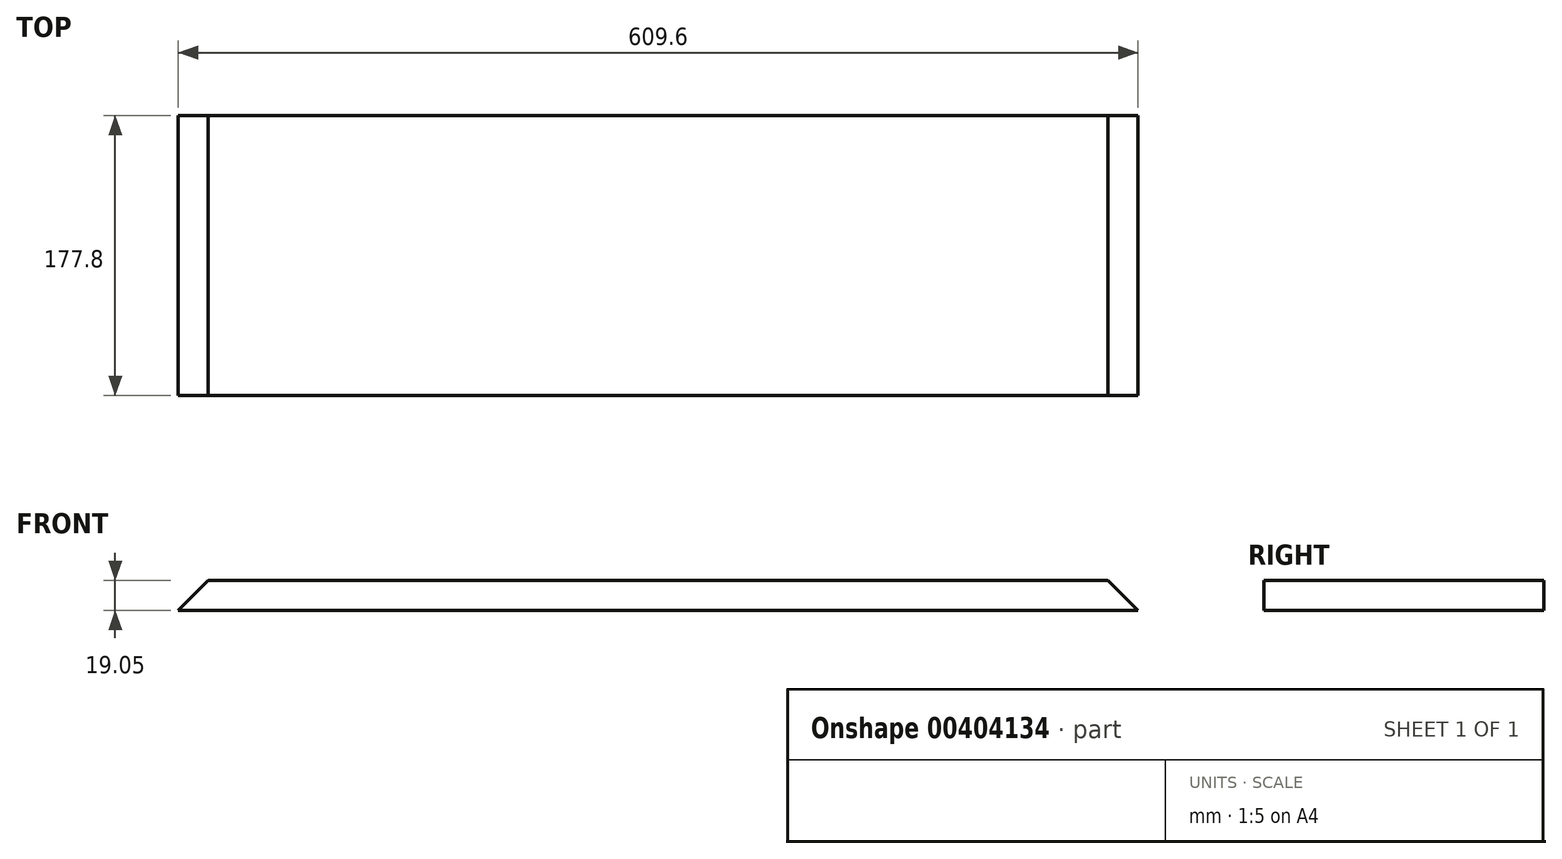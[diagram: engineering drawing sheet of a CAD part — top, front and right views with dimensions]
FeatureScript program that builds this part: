
annotation { "Feature Type Name" : "Feature", "Feature Type Description" : "" }
export const myFeature = defineFeature(function(context is Context, id is Id, definition is map)
    precondition{}
    {
        {
            var Q0;
            Q0=qCreatedBy(makeId("Front.planeOp"),FACE);
            var sketch = newSketch(context, id + "F0", { "sketchPlane" : qUnion([Q0])});
            skLineSegment(sketch, "E0", {"start": v(0, 0) * mm, "end": v(609.6, 0) * mm});
            skLineSegment(sketch, "E1", {"start": v(0, 0) * mm, "end": v(19.05, 19.05) * mm});
            skLineSegment(sketch, "E2", {"start": v(609.6, 0) * mm, "end": v(590.55, 19.05) * mm});
            skLineSegment(sketch, "E3", {"start": v(19.05, 19.05) * mm, "end": v(590.55, 19.05) * mm});
            skSolve(sketch);
        }
        {
            var Q0;
            Q0 = qSketchRegion(id + "F0", true);
            extrude(context, id + "F1", {"entities" : qUnion([Q0]), "endBound" : BoundingType.SYMMETRIC, "depth" : 177.8 * mm});
        }
    });
